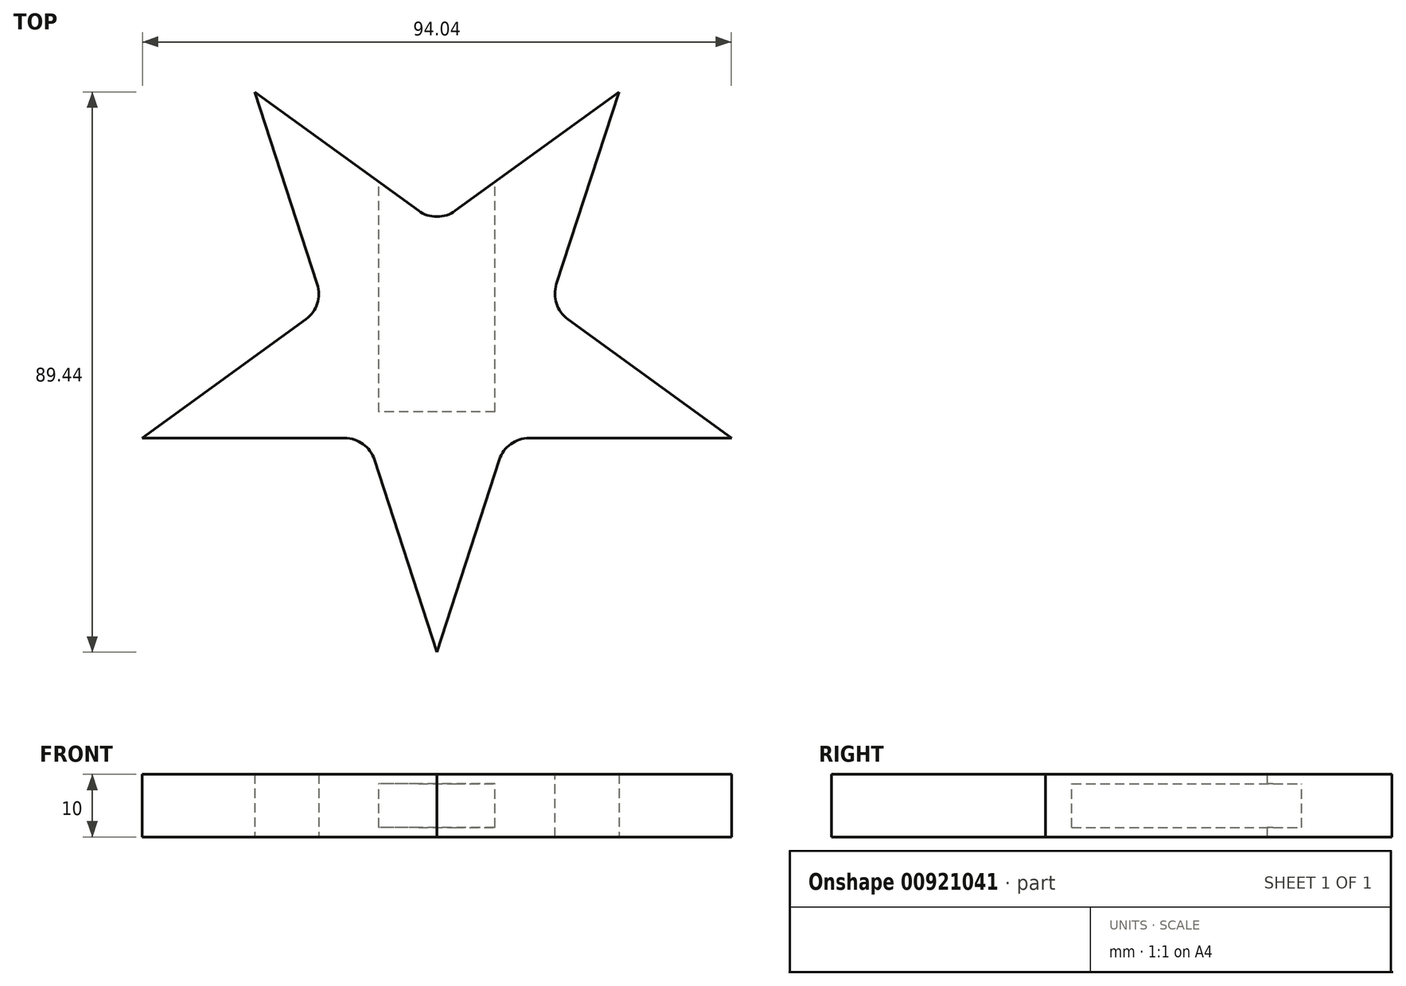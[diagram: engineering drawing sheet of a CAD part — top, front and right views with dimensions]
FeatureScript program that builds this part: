
annotation { "Feature Type Name" : "Feature", "Feature Type Description" : "" }
export const myFeature = defineFeature(function(context is Context, id is Id, definition is map)
    precondition{}
    {
        {
            var Q0;
            Q0=qCreatedBy(makeId("Top.planeOp"),FACE);
            var sketch = newSketch(context, id + "F0", { "sketchPlane" : qUnion([Q0])});
            skCircle(sketch, "E0.cCircle", {"center": v(0, 0) * mm, "radius": 40 * mm, "construction": true});
            skLineSegment(sketch, "E0.0", {"start": v(-29.06, 40) * mm, "end": v(29.06, 40) * mm});
            skLineSegment(sketch, "E0.1", {"start": v(29.06, 40) * mm, "end": v(47.02, -15.28) * mm});
            skLineSegment(sketch, "E0.2", {"start": v(47.02, -15.28) * mm, "end": v(0, -49.44) * mm});
            skLineSegment(sketch, "E0.3", {"start": v(0, -49.44) * mm, "end": v(-47.02, -15.28) * mm});
            skLineSegment(sketch, "E0.4", {"start": v(-47.02, -15.28) * mm, "end": v(-29.06, 40) * mm});
            skPoint(sketch, "E0.0.midPoint", {"position": v(0, 40) * mm});
            skLineSegment(sketch, "E1", {"start": v(-29.06, 40) * mm, "end": v(0, -49.44) * mm});
            skLineSegment(sketch, "E2", {"start": v(0, -49.44) * mm, "end": v(29.06, 40) * mm});
            skLineSegment(sketch, "E3", {"start": v(-47.02, -15.28) * mm, "end": v(29.06, 40) * mm});
            skLineSegment(sketch, "E4", {"start": v(47.02, -15.28) * mm, "end": v(-29.06, 40) * mm});
            skLineSegment(sketch, "E5", {"start": v(-47.02, -15.28) * mm, "end": v(47.02, -15.28) * mm});
            skLineSegment(sketch, "E6", {"start": v(0, 40) * mm, "end": v(0, -8.06) * mm, "construction": true});
            skSolve(sketch);
        }
        {
            var Q0;
            {var subQ1=sQuery(id+"F0.wireOp",EDGE,"E1");var subQ3=sQuery(id+"F0.wireOp",EDGE,"E3");var subQ4=makeQuery(id+"F0.imprint","INTERSECT",VERTEX,{"derivedFrom":[subQ1,subQ3]});Q0=makeQuery(id+"F0.imprint","IMPRINT",FACE,{"disambiguationData":[TD([[makeQuery(id+"F0.imprint","IMPRINT",EDGE,{"disambiguationData":[TD([[subQ4,-1.0]])],"derivedFrom":subQ3}),1.0]])]});}
            var Q1;
            {var subQ1=sQuery(id+"F0.wireOp",EDGE,"E2");var subQ3=sQuery(id+"F0.wireOp",EDGE,"E4");var subQ4=makeQuery(id+"F0.imprint","INTERSECT",VERTEX,{"derivedFrom":[subQ1,subQ3]});Q1=makeQuery(id+"F0.imprint","IMPRINT",FACE,{"disambiguationData":[TD([[makeQuery(id+"F0.imprint","IMPRINT",EDGE,{"disambiguationData":[TD([[subQ4,-1.0]])],"derivedFrom":subQ3}),-1.0]])]});}
            var Q2;
            {var subQ3=sQuery(id+"F0.wireOp",EDGE,"E3");var subQ5=sQuery(id+"F0.wireOp",EDGE,"E1");var subQ6=makeQuery(id+"F0.imprint","INTERSECT",VERTEX,{"derivedFrom":[subQ5,subQ3]});Q2=makeQuery(id+"F0.imprint","IMPRINT",FACE,{"disambiguationData":[TD([[makeQuery(id+"F0.imprint","IMPRINT",EDGE,{"disambiguationData":[TD([[subQ6,-1.0]])],"derivedFrom":subQ5}),1.0]])]});}
            var Q3;
            {var subQ0=sQuery(id+"F0.wireOp",EDGE,"E5");var subQ1=sQuery(id+"F0.wireOp",EDGE,"E2");var subQ2=makeQuery(id+"F0.imprint","INTERSECT",VERTEX,{"derivedFrom":[subQ1,subQ0]});Q3=makeQuery(id+"F0.imprint","IMPRINT",FACE,{"disambiguationData":[TD([[makeQuery(id+"F0.imprint","IMPRINT",EDGE,{"disambiguationData":[TD([[subQ2,-1.0]])],"derivedFrom":subQ1}),-1.0]])]});}
            var Q4;
            {var subQ1=sQuery(id+"F0.wireOp",EDGE,"E1");var subQ3=sQuery(id+"F0.wireOp",EDGE,"E5");var subQ4=makeQuery(id+"F0.imprint","INTERSECT",VERTEX,{"derivedFrom":[subQ1,subQ3]});Q4=makeQuery(id+"F0.imprint","IMPRINT",FACE,{"disambiguationData":[TD([[makeQuery(id+"F0.imprint","IMPRINT",EDGE,{"disambiguationData":[TD([[subQ4,-1.0]])],"derivedFrom":subQ3}),-1.0]])]});}
            var Q5;
            {var subQ0=sQuery(id+"F0.wireOp",EDGE,"E3");var subQ1=sQuery(id+"F0.wireOp",EDGE,"E1");var subQ2=makeQuery(id+"F0.imprint","INTERSECT",VERTEX,{"derivedFrom":[subQ1,subQ0]});Q5=makeQuery(id+"F0.imprint","IMPRINT",FACE,{"disambiguationData":[TD([[makeQuery(id+"F0.imprint","IMPRINT",EDGE,{"disambiguationData":[TD([[subQ2,-1.0]])],"derivedFrom":subQ1}),-1.0]])]});}
            extrude(context, id + "F1", {"entities" : qUnion([Q0, Q1, Q2, Q3, Q4, Q5]), "depth" : 10 * mm, "offsetDistance" : 25 * mm});
        }
        {
            var Q0;
            Q0=makeQuery(id+"F1.opExtrude","CAP_FACE",FACE,{"disambiguationData":[OSD([sQuery(id+"F0.wireOp",EDGE,"E1"),sQuery(id+"F0.wireOp",EDGE,"E2"),sQuery(id+"F0.wireOp",EDGE,"E3"),sQuery(id+"F0.wireOp",EDGE,"E4"),sQuery(id+"F0.wireOp",EDGE,"E5")])],"isStart":false});
            var sketch = newSketch(context, id + "F2", { "sketchPlane" : qUnion([Q0])});
            skLineSegment(sketch, "E7", {"start": v(0, 18.89) * mm, "end": v(0, -11.11) * mm, "construction": true});
            skLineSegment(sketch, "E8", {"start": v(0, -11.11) * mm, "end": v(-9.25, -11.11) * mm});
            skLineSegment(sketch, "E9", {"start": v(-9.25, -11.11) * mm, "end": v(-9.25, 25.6) * mm});
            skLineSegment(sketch, "E10.MirrorCS", {"start": v(9.25, -11.11) * mm, "end": v(9.25, 25.6) * mm});
            skLineSegment(sketch, "E11.MirrorCS", {"start": v(0, -11.11) * mm, "end": v(9.25, -11.11) * mm});
            skSolve(sketch);
        }
        {
            var Q0;
            Q0 = qSketchRegion(id + "F2", true);
            var Q1;
            Q1=makeQuery(id+"F2.imprint","IMPRINT",FACE,{"disambiguationData":[TD([[makeQuery(id+"F2.imprint","IMPRINT",EDGE,{"derivedFrom":sQuery(id+"F2.wireOp",EDGE,"E8")}),-1.0]])]});
            extrude(context, id + "F3", {"entities" : qUnion([Q0, Q1]), "operationType" : NewBodyOperationType.REMOVE, "oppositeDirection" : true, "depth" : 8.5 * mm, "offsetDistance" : 25 * mm, "hasSecondDirection" : true, "secondDirectionOppositeDirection" : true, "secondDirectionDepth" : 1.5 * mm});
        }
        {
            var Q0;
            Q0=makeQuery(id+"F1.opExtrude","SWEPT_EDGE",EDGE,{"disambiguationData":[OSD([sQuery(id+"F0.wireOp",EDGE,"E1"),sQuery(id+"F0.wireOp",EDGE,"E3")])]});
            var Q1;
            Q1=makeQuery(id+"F1.opExtrude","SWEPT_EDGE",EDGE,{"disambiguationData":[OSD([sQuery(id+"F0.wireOp",EDGE,"E1"),sQuery(id+"F0.wireOp",EDGE,"E5")])]});
            var Q2;
            Q2=makeQuery(id+"F1.opExtrude","SWEPT_EDGE",EDGE,{"disambiguationData":[OSD([sQuery(id+"F0.wireOp",EDGE,"E2"),sQuery(id+"F0.wireOp",EDGE,"E5")])]});
            var Q3;
            Q3=makeQuery(id+"F1.opExtrude","SWEPT_EDGE",EDGE,{"disambiguationData":[OSD([sQuery(id+"F0.wireOp",EDGE,"E2"),sQuery(id+"F0.wireOp",EDGE,"E4")])]});
            var Q4;
            {var subQ0=sQuery(id+"F0.wireOp",EDGE,"E4");var subQ1=sQuery(id+"F0.wireOp",EDGE,"E3");var subQ2=sQuery(id+"F0.wireOp",EDGE,"E2");var subQ3=sQuery(id+"F0.wireOp",EDGE,"E1");Q4=makeQuery(id+"F3.boolean.opBoolean","SPLIT",EDGE,{"disambiguationData":[TD([makeQuery(id+"F1.opExtrude","CAP_FACE",FACE,{"disambiguationData":[OSD([subQ3,subQ2,subQ1,subQ0,sQuery(id+"F0.wireOp",EDGE,"E5")])],"isStart":false})])],"derivedFrom":makeQuery(id+"F1.opExtrude","SWEPT_EDGE",EDGE,{"disambiguationData":[OSD([subQ1,subQ0])]})});}
            var Q5;
            {var subQ0=sQuery(id+"F0.wireOp",EDGE,"E4");var subQ1=sQuery(id+"F0.wireOp",EDGE,"E3");var subQ2=sQuery(id+"F0.wireOp",EDGE,"E2");var subQ3=sQuery(id+"F0.wireOp",EDGE,"E1");Q5=makeQuery(id+"F3.boolean.opBoolean","SPLIT",EDGE,{"disambiguationData":[TD([makeQuery(id+"F1.opExtrude","CAP_FACE",FACE,{"disambiguationData":[OSD([subQ3,subQ2,subQ1,subQ0,sQuery(id+"F0.wireOp",EDGE,"E5")])],"isStart":true})])],"derivedFrom":makeQuery(id+"F1.opExtrude","SWEPT_EDGE",EDGE,{"disambiguationData":[OSD([subQ1,subQ0])]})});}
            var Q6;
            Q6=makeQuery(id+"F3.boolean.opBoolean","COPY",EDGE,{"derivedFrom":makeQuery(id+"F3.opExtrude","SWEPT_EDGE",EDGE,{"disambiguationData":[OSD([sQuery(id+"F0.wireOp",EDGE,"E3"),sQuery(id+"F2.wireOp",EDGE,"E10.MirrorCS")])]})});
            var Q7;
            Q7=makeQuery(id+"F3.boolean.opBoolean","COPY",EDGE,{"derivedFrom":makeQuery(id+"F3.opExtrude","SWEPT_EDGE",EDGE,{"disambiguationData":[OSD([sQuery(id+"F0.wireOp",EDGE,"E4"),sQuery(id+"F2.wireOp",EDGE,"E9")])]})});
            fillet(context, id + "F4", {"entities" : qUnion([Q0, Q1, Q2, Q3, Q4, Q5, Q6, Q7]), "radius" : 5 * mm, "tangentPropagation" : true, "allowEdgeOverflow" : false});
        }
    });
